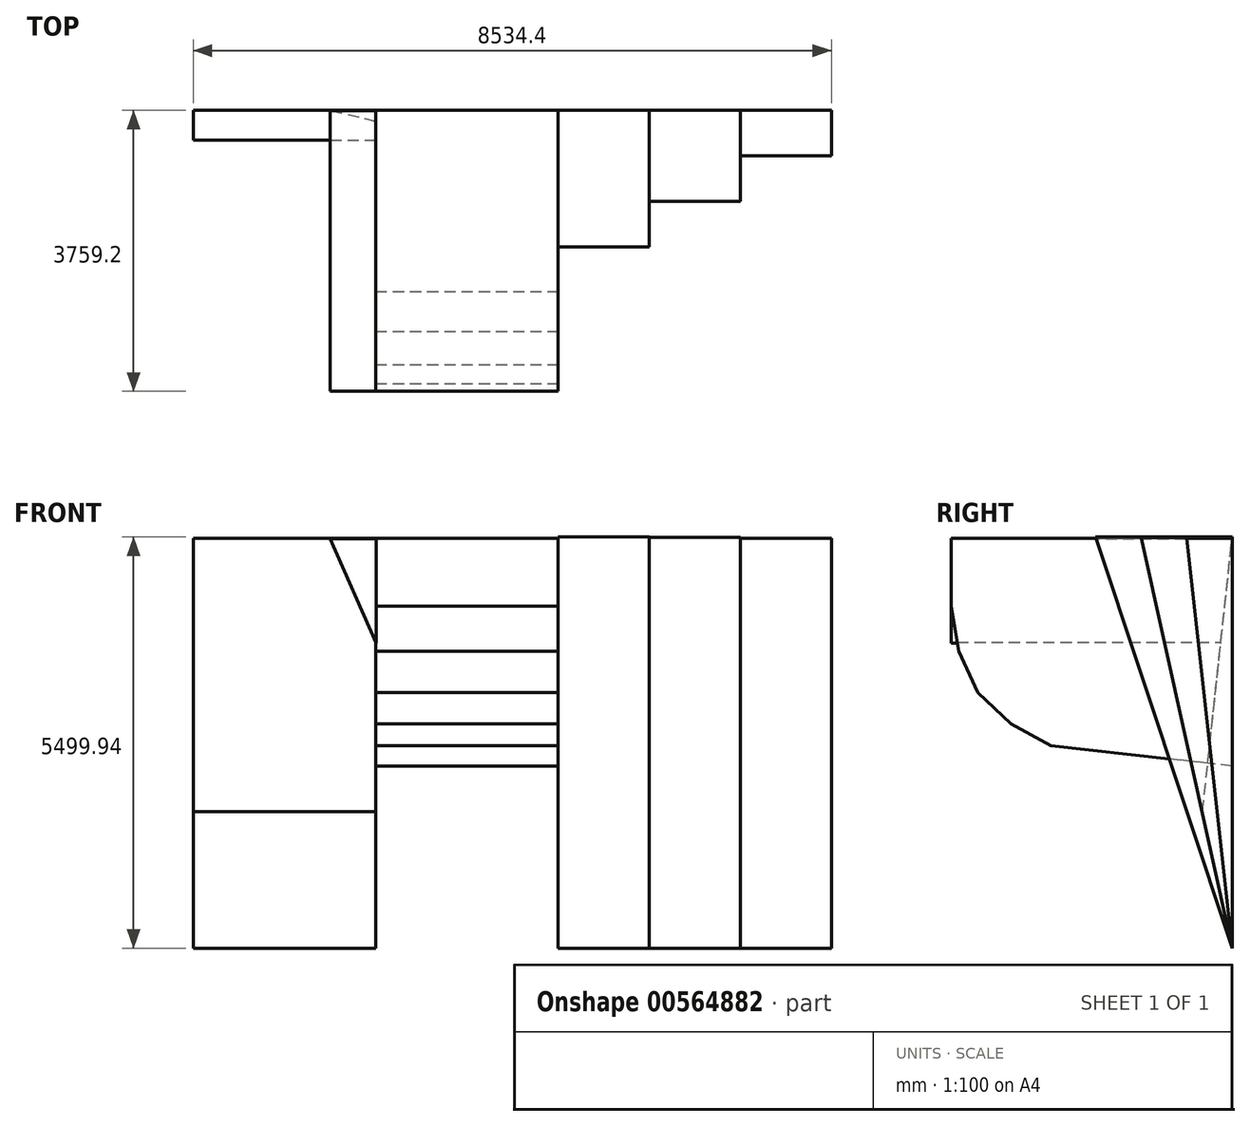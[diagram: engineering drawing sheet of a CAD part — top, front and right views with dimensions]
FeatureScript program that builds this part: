
annotation { "Feature Type Name" : "Feature", "Feature Type Description" : "" }
export const myFeature = defineFeature(function(context is Context, id is Id, definition is map)
    precondition{}
    {
        {
            var Q0;
            Q0=qCreatedBy(makeId("Right.planeOp"),FACE);
            var sketch = newSketch(context, id + "F0", { "sketchPlane" : qUnion([Q0])});
            skLineSegment(sketch, "E0", {"start": v(0, 0) * mm, "end": v(0, 5486.4) * mm});
            skLineSegment(sketch, "E1", {"start": v(0, 5486.4) * mm, "end": v(-609.6, 5486.4) * mm});
            skLineSegment(sketch, "E2", {"start": v(0, 0) * mm, "end": v(-609.6, 5486.4) * mm});
            skSolve(sketch);
        }
        {
            var Q0;
            Q0 = qSketchRegion(id + "F0", true);
            extrude(context, id + "F1", {"entities" : qUnion([Q0]), "depth" : 3657.6 * mm, "offsetDistance" : 25.4 * mm, "hasSecondDirection" : true, "secondDirectionOppositeDirection" : false, "secondDirectionDepth" : 2438.4 * mm});
        }
        {
            var Q0;
            Q0=qCreatedBy(makeId("Right.planeOp"),FACE);
            var sketch = newSketch(context, id + "F2", { "sketchPlane" : qUnion([Q0])});
            skLineSegment(sketch, "E3", {"start": v(0, 0) * mm, "end": v(0, 2438.4) * mm});
            skLineSegment(sketch, "E4", {"start": v(0, 2438.4) * mm, "end": v(-2423.43, 2708.21) * mm});
            skLineSegment(sketch, "E5", {"start": v(-2423.43, 2708.21) * mm, "end": v(-2956.59, 3003.77) * mm});
            skLineSegment(sketch, "E6", {"start": v(-2956.59, 3003.77) * mm, "end": v(-3401.22, 3420.8) * mm});
            skLineSegment(sketch, "E7", {"start": v(-3401.22, 3420.8) * mm, "end": v(-3656.87, 3974.2) * mm});
            skLineSegment(sketch, "E8", {"start": v(-3656.87, 3974.2) * mm, "end": v(-3756.24, 4575.65) * mm});
            skLineSegment(sketch, "E9", {"start": v(-3756.24, 4575.65) * mm, "end": v(-3756.24, 5486.4) * mm});
            skLineSegment(sketch, "E10", {"start": v(-3756.24, 5486.4) * mm, "end": v(0, 5486.4) * mm});
            skLineSegment(sketch, "E11", {"start": v(0, 5486.4) * mm, "end": v(0, 0) * mm});
            skLineSegment(sketch, "E12", {"start": v(0, 2438.4) * mm, "end": v(0, 5486.4) * mm});
            skSolve(sketch);
        }
        {
            var Q0;
            Q0 = qSketchRegion(id + "F2", true);
            extrude(context, id + "F3", {"entities" : qUnion([Q0]), "operationType" : NewBodyOperationType.ADD, "depth" : -2438.4 * mm, "offsetDistance" : 25.4 * mm});
        }
        {
            var Q0;
            Q0=qCreatedBy(makeId("Right.planeOp"),FACE);
            var sketch = newSketch(context, id + "F4", { "sketchPlane" : qUnion([Q0])});
            skLineSegment(sketch, "E13", {"start": v(0, 5498.07) * mm, "end": v(-1219.2, 5498.07) * mm});
            skLineSegment(sketch, "E14", {"start": v(-1219.2, 5498.07) * mm, "end": v(0, 0) * mm});
            skLineSegment(sketch, "E15", {"start": v(0, 0) * mm, "end": v(0, 5498.07) * mm});
            skSolve(sketch);
        }
        {
            var Q0;
            Q0 = qSketchRegion(id + "F4", true);
            extrude(context, id + "F5", {"entities" : qUnion([Q0]), "operationType" : NewBodyOperationType.ADD, "depth" : 2438.4 * mm, "offsetDistance" : 25.4 * mm, "hasSecondDirection" : true, "secondDirectionOppositeDirection" : false, "secondDirectionDepth" : 1219.2 * mm});
        }
        {
            var Q0;
            Q0=qCreatedBy(makeId("Right.planeOp"),FACE);
            var sketch = newSketch(context, id + "F6", { "sketchPlane" : qUnion([Q0])});
            skLineSegment(sketch, "E16", {"start": v(0, 5499.94) * mm, "end": v(-1828.8, 5499.94) * mm});
            skLineSegment(sketch, "E17", {"start": v(-1828.8, 5499.94) * mm, "end": v(0, 0) * mm});
            skLineSegment(sketch, "E18", {"start": v(0, 0) * mm, "end": v(0, 5499.94) * mm});
            skSolve(sketch);
        }
        {
            var Q0;
            Q0 = qSketchRegion(id + "F6", true);
            extrude(context, id + "F7", {"entities" : qUnion([Q0]), "depth" : 1219.2 * mm, "offsetDistance" : 25.4 * mm});
        }
        {
            var Q0;
            Q0=qCreatedBy(makeId("Right.planeOp"),FACE);
            var sketch = newSketch(context, id + "F8", { "sketchPlane" : qUnion([Q0])});
            skLineSegment(sketch, "E19", {"start": v(0, 0) * mm, "end": v(0, 5486.4) * mm});
            skLineSegment(sketch, "E20", {"start": v(0, 5486.4) * mm, "end": v(0, 1828.8) * mm});
            skLineSegment(sketch, "E21", {"start": v(0, 1828.8) * mm, "end": v(-395.93, 1828.8) * mm});
            skLineSegment(sketch, "E22", {"start": v(-395.93, 1828.8) * mm, "end": v(0, 5486.4) * mm});
            skLineSegment(sketch, "E23", {"start": v(-395.93, 1828.8) * mm, "end": v(0, 0) * mm});
            skSolve(sketch);
        }
        {
            var Q0;
            Q0 = qSketchRegion(id + "F8", true);
            extrude(context, id + "F9", {"entities" : qUnion([Q0]), "operationType" : NewBodyOperationType.ADD, "oppositeDirection" : true, "depth" : 4876.8 * mm, "offsetDistance" : 25.4 * mm, "hasSecondDirection" : true, "secondDirectionOppositeDirection" : true, "secondDirectionDepth" : 2438.4 * mm});
        }
        {
            var Q0;
            Q0=qCreatedBy(makeId("Front.planeOp"),FACE);
            var sketch = newSketch(context, id + "F10", { "sketchPlane" : qUnion([Q0])});
            skLineSegment(sketch, "E24", {"start": v(-2433.46, 4083.14) * mm, "end": v(-3043.06, 5479.91) * mm});
            skLineSegment(sketch, "E25", {"start": v(-3043.06, 5479.91) * mm, "end": v(-2433.46, 5479.91) * mm});
            skLineSegment(sketch, "E26", {"start": v(-2433.46, 5479.91) * mm, "end": v(-2433.46, 4083.14) * mm});
            skSolve(sketch);
        }
        {
            var Q0;
            Q0 = qSketchRegion(id + "F10", true);
            extrude(context, id + "F11", {"entities" : qUnion([Q0]), "operationType" : NewBodyOperationType.ADD, "depth" : 3759.2 * mm, "offsetDistance" : 25.4 * mm});
        }
    });
